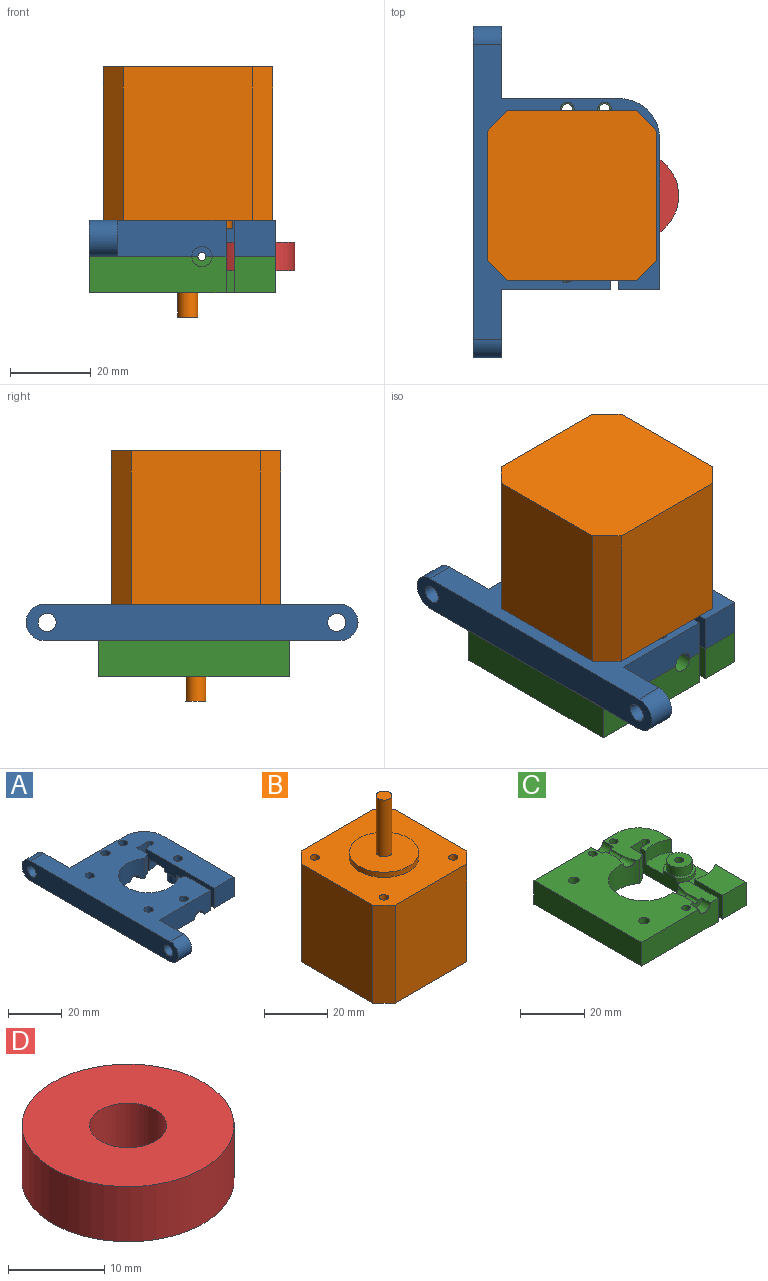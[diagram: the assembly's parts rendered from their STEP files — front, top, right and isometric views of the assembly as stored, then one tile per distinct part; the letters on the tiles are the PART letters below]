
ASSEMBLY  parts=4 mates=3
PART A: 50 faces, bbox 46.2x82.3x9 mm
  f0: plane 73.31x26.93mm, normal (0,0,-1), area 1154.6mm2, adj f3,f8,f9,f10,f15,f17,f21,f22
  f1: plane 14.38x4.98mm, normal (0,0,-1), area 60mm2, adj f3,f6,f10,f34,f35,f36,f37,f48
  f2: plane 17.27x15.32mm, normal (0,0,-1), area 172.9mm2, adj f3,f4,f5,f7,f8,f11,f12,f13
  f3: cylinder r=11.1mm len=22.2mm, axis (0,0,-1), area 432.3mm2, adj f0,f1,f2,f19,f33,f36,f48,f49
  f4: plane 36.35x9mm, normal (-1,0,0), area 219.3mm2, adj f2,f13,f14,f18,f19,f23,f24,f25
  f5: plane 37.28x9mm, normal (1,0,0), area 230.1mm2, adj f2,f14,f18,f19,f20,f23,f25,f26
  f6: plane 13.04x9mm, normal (1,0,0), area 111.2mm2, adj f1,f10,f19,f39,f48
  f7: plane 9x5.51mm, normal (1,0,0), area 49.5mm2, adj f2,f11,f19,f49
  f8: plane 29.2x9mm, normal (0,1,0), area 252.8mm2, adj f0,f2,f19,f20,f32,f43
  f9: plane 82.31x9mm, normal (-1,0,0), area 691.6mm2, adj f0,f19,f44,f45,f46,f47
  f10: plane 26.91x9mm, normal (0,-1,0), area 232.2mm2, adj f0,f1,f6,f19,f37,f42
  f11: plane 9x5.65mm, normal (0,-1,0), area 50.9mm2, adj f2,f7,f12,f19
  f12: cylinder r=1.22mm len=9mm, axis (0,0,1), area 34.6mm2, adj f2,f11,f13,f19
  f13: plane 9x3.65mm, normal (0,1,0), area 32.9mm2, adj f2,f4,f12,f19
  f14: plane 10.29x9mm, normal (0,-1,0), area 92.6mm2, adj f4,f5,f18,f19
  f15: cylinder r=1.7mm len=9mm, axis (0,0,1), area 96.1mm2, adj f0,f19
  f16: cylinder r=1.7mm len=9mm, axis (0,0,1), area 96.1mm2, adj f2,f19
  f17: cylinder r=1.7mm len=9mm, axis (0,0,1), area 96.1mm2, adj f0,f19
  f18: plane 13.53x10.29mm, normal (0,0,-1), area 124.8mm2, adj f4,f5,f14,f25
  f19: plane 73.31x46.2mm, normal (0,0,1), area 1816.6mm2, adj f3,f4,f5,f6,f7,f8,f9,f10
  f20: cylinder r=10mm len=10mm, axis (0,0,1), area 141.4mm2, adj f2,f5,f8,f19
  f21: cylinder r=1.7mm len=9mm, axis (0,0,-1), area 96.1mm2, adj f0,f19
  f22: cylinder r=1.7mm len=9mm, axis (0,0,-1), area 96.1mm2, adj f0,f19
  f23: cylinder r=11.5mm len=10.29mm, axis (0,0,-1), area 53.7mm2, adj f2,f4,f5,f26
  f24: cylinder r=5mm len=10mm, axis (0,0,-1), area 37.6mm2, adj f4,f26,f28
  f25: cylinder r=11.5mm len=10.29mm, axis (0,0,-1), area 53.7mm2, adj f4,f5,f18,f26
  f26: plane 23x10.29mm, normal (0,0,-1), area 152.7mm2, adj f4,f5,f23,f24,f25
  f27: cylinder r=4mm len=8mm, axis (0,0,-1), area 88mm2, adj f28,f29
  f28: plane 10x9.02mm, normal (0,0,-1), area 24.3mm2, adj f4,f24,f27
  f29: plane 8x8mm, normal (0,0,-1), area 41.2mm2, adj f27,f41
  f30: plane 5.04x2.52mm, normal (0,1,0), area 8.4mm2, adj f0,f2,f31,f32
  f31: cylinder r=1mm len=4.98mm, axis (0,-1,0), area 15.6mm2, adj f0,f2,f30,f33
  f32: cylinder r=2.52mm len=5.04mm, axis (0,-1,0), area 37.6mm2, adj f0,f2,f8,f30
  f33: cone r=1mm half-angle=13.3deg, axis (0,-1,0), area 19mm2, adj f0,f2,f3,f31
  f34: cylinder r=1mm len=4.98mm, axis (0,-1,0), area 15.6mm2, adj f0,f1,f35,f36
  f35: plane 5.04x2.52mm, normal (0,-1,0), area 8.4mm2, adj f0,f1,f34,f37
  f36: cone r=1mm half-angle=13.3deg, axis (0,1,0), area 19mm2, adj f0,f1,f3,f34
  f37: cylinder r=2.52mm len=5.04mm, axis (0,-1,0), area 30.1mm2, adj f0,f1,f10,f35
  f38: plane 2.8x2.8mm, normal (1,0,0), area 6.2mm2, adj f39
  f39: cylinder r=1.4mm len=7.71mm, axis (1,0,0), area 67.8mm2, adj f6,f38
  f40: cylinder r=1.7mm len=10.29mm, axis (1,0,0), area 109.9mm2, adj f4,f5
  f41: cylinder r=1.7mm len=9mm, axis (0,0,-1), area 96.1mm2, adj f19,f29
  f42: plane 17.03x9mm, normal (1,0,0), area 128.7mm2, adj f0,f10,f19,f44,f46
  f43: plane 18x9mm, normal (1,0,0), area 137.4mm2, adj f0,f8,f19,f45,f47
  f44: cylinder r=2.25mm len=7mm, axis (1,0,0), area 99mm2, adj f9,f42
  f45: cylinder r=2.25mm len=7mm, axis (1,0,0), area 99mm2, adj f9,f43
  f46: cylinder r=4.5mm len=9mm, axis (1,0,0), area 99mm2, adj f0,f9,f19,f42
  f47: cylinder r=4.5mm len=9mm, axis (-1,0,0), area 99mm2, adj f0,f9,f19,f43
  f48: plane 9x2.71mm, normal (0.44,0.9,0), area 27.2mm2, adj f1,f3,f6,f19
  f49: plane 9x2.71mm, normal (0.44,-0.9,0), area 27.2mm2, adj f2,f3,f7,f19
PART B: 22 faces, bbox 42x42x62 mm
  f0: plane 38x32mm, normal (-1,0,0), area 1216mm2, adj f4,f5,f8,f9
  f1: plane 38x32mm, normal (0,-1,0), area 1216mm2, adj f4,f5,f7,f9
  f2: plane 38x32mm, normal (1,0,0), area 1216mm2, adj f4,f5,f6,f7
  f3: plane 38x32mm, normal (0,1,0), area 1216mm2, adj f4,f5,f6,f8
  f4: plane 42x42mm, normal (0,0,1), area 1305.6mm2, adj f0,f1,f2,f3,f6,f7,f8,f9
  f5: plane 42x42mm, normal (0,0,-1), area 1714mm2, adj f0,f1,f2,f3,f6,f7,f8,f9
  f6: plane 38x5mm, normal (0.71,0.71,0), area 268.7mm2, adj f2,f3,f4,f5
  f7: plane 38x5mm, normal (0.71,-0.71,0), area 268.7mm2, adj f1,f2,f4,f5
  f8: plane 38x5mm, normal (-0.71,0.71,0), area 268.7mm2, adj f0,f3,f4,f5
  f9: plane 38x5mm, normal (-0.71,-0.71,0), area 268.7mm2, adj f0,f1,f4,f5
  f10: cylinder r=11mm len=22mm, axis (0,0,-1), area 138.2mm2, adj f4,f11
  f11: plane 22x22mm, normal (0,0,1), area 360.5mm2, adj f10,f12
  f12: cylinder r=2.5mm len=22mm, axis (0,0,-1), area 345.6mm2, adj f11,f13
  f13: plane 5x5mm, normal (0,0,1), area 19.6mm2, adj f12
  f14: cylinder r=1.5mm len=25mm, axis (0,0,1), area 235.6mm2, adj f4,f15
  f15: plane 3x3mm, normal (0,0,1), area 7.1mm2, adj f14
  f16: cylinder r=1.5mm len=25mm, axis (0,0,1), area 235.6mm2, adj f4,f17
  f17: plane 3x3mm, normal (0,0,1), area 7.1mm2, adj f16
  f18: cylinder r=1.5mm len=25mm, axis (0,0,1), area 235.6mm2, adj f4,f19
  f19: plane 3x3mm, normal (0,0,1), area 7.1mm2, adj f18
  f20: cylinder r=1.5mm len=25mm, axis (0,0,1), area 235.6mm2, adj f4,f21
  f21: plane 3x3mm, normal (0,0,1), area 7.1mm2, adj f20
PART C: 44 faces, bbox 46.2x47.3x9 mm
  f0: plane 47.28x26.93mm, normal (0,0,1), area 979.1mm2, adj f3,f7,f8,f9,f16,f18,f21,f22
  f1: plane 14.38x4.98mm, normal (0,0,1), area 60mm2, adj f3,f6,f9,f33,f34,f35,f36,f43
  f2: plane 17.27x15.32mm, normal (0,0,1), area 176.2mm2, adj f3,f4,f7,f10,f11,f12,f13,f15
  f3: cylinder r=11.1mm len=22.2mm, axis (0,0,1), area 432.3mm2, adj f0,f1,f2,f20,f32,f33,f42,f43
  f4: plane 36.35x9mm, normal (-1,0,0), area 219.3mm2, adj f2,f5,f13,f14,f19,f20,f23,f24
  f5: cylinder r=5mm len=10mm, axis (0,0,1), area 37.6mm2, adj f4,f25,f26
  f6: plane 13.04x9mm, normal (1,0,0), area 111.2mm2, adj f1,f9,f20,f38,f43
  f7: plane 36.2x9mm, normal (0,1,0), area 315.8mm2, adj f0,f2,f8,f20,f29,f37
  f8: plane 47.28x9mm, normal (-1,0,0), area 425.5mm2, adj f0,f7,f9,f20
  f9: plane 33.91x9mm, normal (0,-1,0), area 295.2mm2, adj f0,f1,f6,f8,f20,f36
  f10: plane 9x5.51mm, normal (1,0,0), area 49.5mm2, adj f2,f11,f20,f42
  f11: plane 9x5.65mm, normal (0,-1,0), area 50.9mm2, adj f2,f10,f12,f20
  f12: cylinder r=1.22mm len=9mm, axis (0,0,-1), area 34.6mm2, adj f2,f11,f13,f20
  f13: plane 9x3.65mm, normal (0,1,0), area 32.9mm2, adj f2,f4,f12,f20
  f14: plane 10.29x9mm, normal (0,-1,0), area 92.6mm2, adj f4,f17,f19,f20
  f15: cylinder r=1.35mm len=9mm, axis (0,0,-1), area 76.3mm2, adj f2,f20
  f16: cylinder r=1.35mm len=9mm, axis (0,0,-1), area 76.3mm2, adj f0,f20
  f17: plane 37.28x9mm, normal (1,0,0), area 230.1mm2, adj f2,f14,f19,f20,f23,f24,f25,f37
  f18: cylinder r=1.35mm len=9mm, axis (0,0,-1), area 76.3mm2, adj f0,f20
  f19: plane 13.53x10.29mm, normal (0,0,1), area 124.8mm2, adj f4,f14,f17,f24
  f20: plane 47.28x46.2mm, normal (0,0,-1), area 1647.4mm2, adj f3,f4,f6,f7,f8,f9,f10,f11
  f21: cylinder r=1.7mm len=9mm, axis (0,0,1), area 96.1mm2, adj f0,f20
  f22: cylinder r=1.7mm len=9mm, axis (0,0,1), area 96.1mm2, adj f0,f20
  f23: cylinder r=11.5mm len=10.29mm, axis (0,0,1), area 53.7mm2, adj f2,f4,f17,f25
  f24: cylinder r=11.5mm len=10.29mm, axis (0,0,1), area 53.7mm2, adj f4,f17,f19,f25
  f25: plane 23x10.29mm, normal (0,0,1), area 152.7mm2, adj f4,f5,f17,f23,f24
  f26: plane 10x9.02mm, normal (0,0,1), area 24.3mm2, adj f4,f5,f27
  f27: cylinder r=4mm len=8mm, axis (0,0,1), area 88mm2, adj f26,f28
  f28: plane 8x8mm, normal (0,0,1), area 44.1mm2, adj f27,f41
  f29: cylinder r=2.52mm len=5.04mm, axis (0,-1,0), area 37.6mm2, adj f0,f2,f7,f30
  f30: plane 5.04x2.52mm, normal (0,1,0), area 8.4mm2, adj f0,f2,f29,f31
  f31: cylinder r=1mm len=4.98mm, axis (0,-1,0), area 15.6mm2, adj f0,f2,f30,f32
  f32: cone r=1mm half-angle=13.3deg, axis (0,-1,0), area 19mm2, adj f0,f2,f3,f31
  f33: cone r=1mm half-angle=13.3deg, axis (0,1,0), area 19mm2, adj f0,f1,f3,f34
  f34: cylinder r=1mm len=4.98mm, axis (0,-1,0), area 15.6mm2, adj f0,f1,f33,f35
  f35: plane 5.04x2.52mm, normal (0,-1,0), area 8.4mm2, adj f0,f1,f34,f36
  f36: cylinder r=2.52mm len=5.04mm, axis (0,-1,0), area 30.1mm2, adj f0,f1,f9,f35
  f37: cylinder r=10mm len=10mm, axis (0,0,-1), area 141.4mm2, adj f2,f7,f17,f20
  f38: cylinder r=1.4mm len=7.71mm, axis (1,0,0), area 67.8mm2, adj f6,f39
  f39: plane 2.8x2.8mm, normal (1,0,0), area 6.2mm2, adj f38
  f40: cylinder r=1.7mm len=10.29mm, axis (1,0,0), area 109.9mm2, adj f4,f17
  f41: cylinder r=1.4mm len=9mm, axis (0,0,1), area 79.2mm2, adj f20,f28
  f42: plane 9x2.71mm, normal (0.44,-0.9,0), area 27.2mm2, adj f2,f3,f10,f20
  f43: plane 9x2.71mm, normal (0.44,0.9,0), area 27.2mm2, adj f1,f3,f6,f20
PART D: 4 faces, bbox 22x22x7 mm
  f0: cylinder r=4mm len=8mm, axis (0,0,-1), area 175.9mm2, adj f2,f3
  f1: cylinder r=11mm len=22mm, axis (0,0,-1), area 483.8mm2, adj f2,f3
  f2: plane 22x22mm, normal (0,0,1), area 329.9mm2, adj f0,f1
  f3: plane 22x22mm, normal (0,0,-1), area 329.9mm2, adj f0,f1
PLACE A t=(-37.06,-1.17,34.2)mm
PLACE B rot(axis=(0.71,-0.71,0),180deg) t=(-16.06,25.66,90.2)mm
PLACE C t=(-37.06,-1.17,34.2)mm
PLACE D t=(-21.56,4.66,39.7)mm
MATE fastened D.f0 <-> C.f5  axis (0,0,-1) through (-21.56,4.66,39.7)mm
MATE fastened B.f20 <-> A.f22  axis (0,0,-1) through (-52.56,20.16,52.2)mm
MATE fastened D.f0 <-> A.f23  axis (0,0,1) through (-21.56,4.66,46.7)mm
